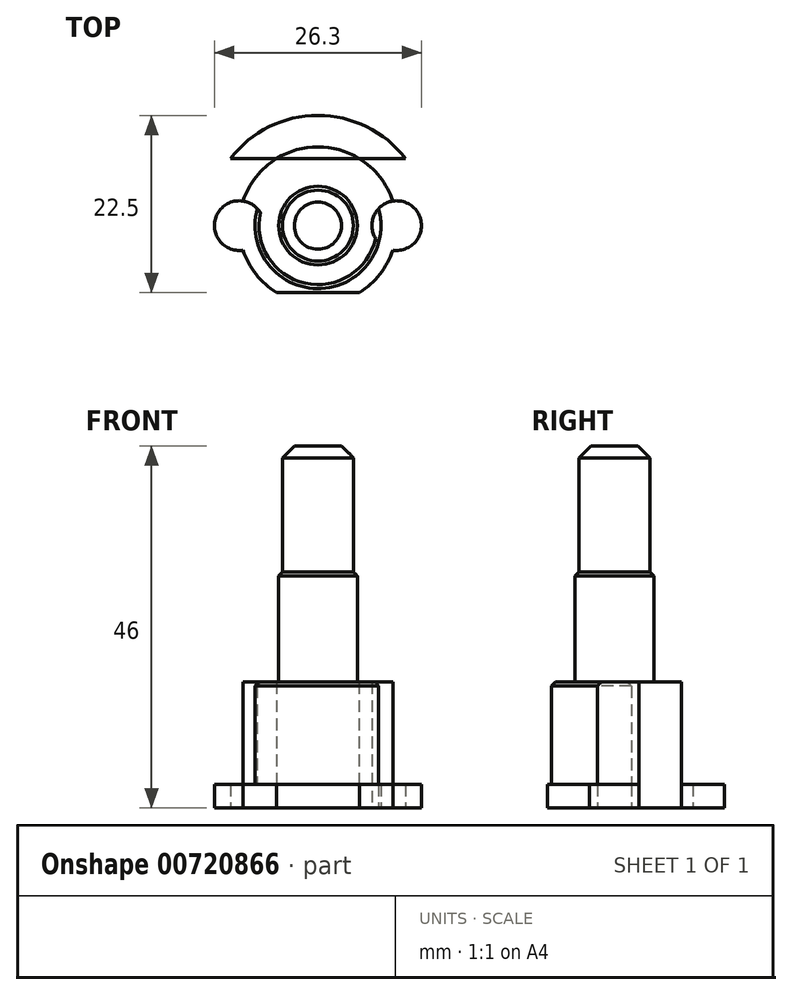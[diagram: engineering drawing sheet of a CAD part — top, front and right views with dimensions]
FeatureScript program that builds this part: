
annotation { "Feature Type Name" : "Feature", "Feature Type Description" : "" }
export const myFeature = defineFeature(function(context is Context, id is Id, definition is map)
    precondition{}
    {
        {
            var Q0;
            Q0=qCreatedBy(makeId("Top.planeOp"),FACE);
            var sketch = newSketch(context, id + "F0", { "sketchPlane" : qUnion([Q0])});
            skCircle(sketch, "E0", {"center": v(0, 0) * mm, "radius": 14 * mm});
            skCircle(sketch, "E1", {"center": v(0, 0) * mm, "radius": 10 * mm});
            skCircle(sketch, "E2", {"center": v(-10, 0) * mm, "radius": 3.15 * mm});
            skCircle(sketch, "E3", {"center": v(-10, 0) * mm, "radius": 1.7 * mm});
            skCircle(sketch, "E4.MirrorC", {"center": v(10, 0) * mm, "radius": 3.15 * mm});
            skCircle(sketch, "E5.MirrorC", {"center": v(10, 0) * mm, "radius": 1.7 * mm});
            skPoint(sketch, "E6", {"position": v(0, 8.5) * mm});
            skPoint(sketch, "E7", {"position": v(0, -8.5) * mm});
            skLineSegment(sketch, "E8", {"start": v(-11.11, 8.52) * mm, "end": v(11.11, 8.52) * mm});
            skLineSegment(sketch, "E9", {"start": v(11.12, -8.5) * mm, "end": v(-11.8, -8.5) * mm});
            skCircle(sketch, "E10", {"center": v(0, 0) * mm, "radius": 8 * mm});
            skSolve(sketch);
        }
        {
            var Q0;
            {var subQ1=sQuery(id+"F0.wireOp",EDGE,"E1");var subQ3=sQuery(id+"F0.wireOp",EDGE,"E4.MirrorC");var subQ11=makeQuery(id+"F0.imprint","INTERSECT",VERTEX,{"disambiguationData":[OD(0.0)],"derivedFrom":[subQ1,subQ3]});Q0=makeQuery(id+"F0.imprint","IMPRINT",FACE,{"disambiguationData":[TD([[makeQuery(id+"F0.imprint","IMPRINT",EDGE,{"disambiguationData":[TD([[subQ11,-1.0]])],"derivedFrom":subQ1}),1.0]])]});}
            var Q1;
            {var subQ0=sQuery(id+"F0.wireOp",EDGE,"E2");var subQ1=sQuery(id+"F0.wireOp",EDGE,"E1");var subQ2=makeQuery(id+"F0.imprint","INTERSECT",VERTEX,{"disambiguationData":[OD(0.0)],"derivedFrom":[subQ1,subQ0]});Q1=makeQuery(id+"F0.imprint","IMPRINT",FACE,{"disambiguationData":[TD([[makeQuery(id+"F0.imprint","IMPRINT",EDGE,{"disambiguationData":[TD([[subQ2,-1.0]])],"derivedFrom":subQ1}),1.0]])]});}
            var Q2;
            {var subQ0=sQuery(id+"F0.wireOp",EDGE,"E3");var subQ1=sQuery(id+"F0.wireOp",EDGE,"E1");var subQ2=makeQuery(id+"F0.imprint","INTERSECT",VERTEX,{"disambiguationData":[OD(0.0)],"derivedFrom":[subQ1,subQ0]});Q2=makeQuery(id+"F0.imprint","IMPRINT",FACE,{"disambiguationData":[TD([[makeQuery(id+"F0.imprint","IMPRINT",EDGE,{"disambiguationData":[TD([[subQ2,-1.0]])],"derivedFrom":subQ1}),1.0]])]});}
            var Q3;
            {var subQ0=sQuery(id+"F0.wireOp",EDGE,"E3");var subQ1=sQuery(id+"F0.wireOp",EDGE,"E1");var subQ2=makeQuery(id+"F0.imprint","INTERSECT",VERTEX,{"disambiguationData":[OD(0.0)],"derivedFrom":[subQ1,subQ0]});Q3=makeQuery(id+"F0.imprint","IMPRINT",FACE,{"disambiguationData":[TD([[makeQuery(id+"F0.imprint","IMPRINT",EDGE,{"disambiguationData":[TD([[subQ2,-1.0]])],"derivedFrom":subQ1}),-1.0]])]});}
            var Q4;
            {var subQ0=sQuery(id+"F0.wireOp",EDGE,"E2");var subQ1=sQuery(id+"F0.wireOp",EDGE,"E1");var subQ2=makeQuery(id+"F0.imprint","INTERSECT",VERTEX,{"disambiguationData":[OD(0.0)],"derivedFrom":[subQ1,subQ0]});Q4=makeQuery(id+"F0.imprint","IMPRINT",FACE,{"disambiguationData":[TD([[makeQuery(id+"F0.imprint","IMPRINT",EDGE,{"disambiguationData":[TD([[subQ2,-1.0]])],"derivedFrom":subQ1}),-1.0]])]});}
            var Q5;
            {var subQ0=sQuery(id+"F0.wireOp",EDGE,"E8");var subQ6=sQuery(id+"F0.wireOp",EDGE,"E0");var subQ10=makeQuery(id+"F0.imprint","INTERSECT",VERTEX,{"disambiguationData":[OD(0.0)],"derivedFrom":[subQ6,subQ0]});Q5=makeQuery(id+"F0.imprint","IMPRINT",FACE,{"disambiguationData":[TD([[makeQuery(id+"F0.imprint","IMPRINT",EDGE,{"disambiguationData":[TD([[subQ10,-1.0]])],"derivedFrom":subQ6}),1.0]])]});}
            var Q6;
            {var subQ4=sQuery(id+"F0.wireOp",EDGE,"E8");var subQ7=sQuery(id+"F0.wireOp",EDGE,"E0");var subQ10=makeQuery(id+"F0.imprint","INTERSECT",VERTEX,{"disambiguationData":[OD(1.0)],"derivedFrom":[subQ7,subQ4]});Q6=makeQuery(id+"F0.imprint","IMPRINT",FACE,{"disambiguationData":[TD([[makeQuery(id+"F0.imprint","IMPRINT",EDGE,{"disambiguationData":[TD([[subQ10,1.0]])],"derivedFrom":subQ7}),1.0]])]});}
            var Q7;
            {var subQ0=sQuery(id+"F0.wireOp",EDGE,"E5.MirrorC");var subQ1=sQuery(id+"F0.wireOp",EDGE,"E1");var subQ2=makeQuery(id+"F0.imprint","INTERSECT",VERTEX,{"disambiguationData":[OD(0.0)],"derivedFrom":[subQ1,subQ0]});Q7=makeQuery(id+"F0.imprint","IMPRINT",FACE,{"disambiguationData":[TD([[makeQuery(id+"F0.imprint","IMPRINT",EDGE,{"disambiguationData":[TD([[subQ2,1.0]])],"derivedFrom":subQ1}),-1.0]])]});}
            var Q8;
            {var subQ0=sQuery(id+"F0.wireOp",EDGE,"E4.MirrorC");var subQ1=sQuery(id+"F0.wireOp",EDGE,"E1");var subQ2=makeQuery(id+"F0.imprint","INTERSECT",VERTEX,{"disambiguationData":[OD(0.0)],"derivedFrom":[subQ1,subQ0]});Q8=makeQuery(id+"F0.imprint","IMPRINT",FACE,{"disambiguationData":[TD([[makeQuery(id+"F0.imprint","IMPRINT",EDGE,{"disambiguationData":[TD([[subQ2,1.0]])],"derivedFrom":subQ1}),-1.0]])]});}
            var Q9;
            {var subQ0=sQuery(id+"F0.wireOp",EDGE,"E5.MirrorC");var subQ1=sQuery(id+"F0.wireOp",EDGE,"E1");var subQ2=makeQuery(id+"F0.imprint","INTERSECT",VERTEX,{"disambiguationData":[OD(0.0)],"derivedFrom":[subQ1,subQ0]});Q9=makeQuery(id+"F0.imprint","IMPRINT",FACE,{"disambiguationData":[TD([[makeQuery(id+"F0.imprint","IMPRINT",EDGE,{"disambiguationData":[TD([[subQ2,1.0]])],"derivedFrom":subQ1}),1.0]])]});}
            var Q10;
            {var subQ0=sQuery(id+"F0.wireOp",EDGE,"E4.MirrorC");var subQ1=sQuery(id+"F0.wireOp",EDGE,"E1");var subQ2=makeQuery(id+"F0.imprint","INTERSECT",VERTEX,{"disambiguationData":[OD(0.0)],"derivedFrom":[subQ1,subQ0]});Q10=makeQuery(id+"F0.imprint","IMPRINT",FACE,{"disambiguationData":[TD([[makeQuery(id+"F0.imprint","IMPRINT",EDGE,{"disambiguationData":[TD([[subQ2,1.0]])],"derivedFrom":subQ1}),1.0]])]});}
            var Q11;
            {var subQ1=sQuery(id+"F0.wireOp",EDGE,"E1");var subQ7=sQuery(id+"F0.wireOp",EDGE,"E2");var subQ8=makeQuery(id+"F0.imprint","INTERSECT",VERTEX,{"disambiguationData":[OD(1.0)],"derivedFrom":[subQ1,subQ7]});Q11=makeQuery(id+"F0.imprint","IMPRINT",FACE,{"disambiguationData":[TD([[makeQuery(id+"F0.imprint","IMPRINT",EDGE,{"disambiguationData":[TD([[subQ8,-1.0]])],"derivedFrom":subQ1}),1.0]])]});}
            var Q12;
            {var subQ0=sQuery(id+"F0.wireOp",EDGE,"E10");var subQ1=sQuery(id+"F0.wireOp",EDGE,"E2");var subQ2=makeQuery(id+"F0.imprint","INTERSECT",VERTEX,{"disambiguationData":[OD(0.0)],"derivedFrom":[subQ1,subQ0]});Q12=makeQuery(id+"F0.imprint","IMPRINT",FACE,{"disambiguationData":[TD([[makeQuery(id+"F0.imprint","IMPRINT",EDGE,{"disambiguationData":[TD([[subQ2,1.0]])],"derivedFrom":subQ1}),-1.0]])]});}
            var Q13;
            {var subQ0=sQuery(id+"F0.wireOp",EDGE,"E10");var subQ1=sQuery(id+"F0.wireOp",EDGE,"E4.MirrorC");var subQ2=makeQuery(id+"F0.imprint","INTERSECT",VERTEX,{"disambiguationData":[OD(0.0)],"derivedFrom":[subQ1,subQ0]});Q13=makeQuery(id+"F0.imprint","IMPRINT",FACE,{"disambiguationData":[TD([[makeQuery(id+"F0.imprint","IMPRINT",EDGE,{"disambiguationData":[TD([[subQ2,1.0]])],"derivedFrom":subQ1}),-1.0]])]});}
            var Q14;
            {var subQ0=sQuery(id+"F0.wireOp",EDGE,"E10");var subQ1=sQuery(id+"F0.wireOp",EDGE,"E2");var subQ2=makeQuery(id+"F0.imprint","INTERSECT",VERTEX,{"disambiguationData":[OD(0.0)],"derivedFrom":[subQ1,subQ0]});Q14=makeQuery(id+"F0.imprint","IMPRINT",FACE,{"disambiguationData":[TD([[makeQuery(id+"F0.imprint","IMPRINT",EDGE,{"disambiguationData":[TD([[subQ2,1.0]])],"derivedFrom":subQ1}),1.0]])]});}
            extrude(context, id + "F1", {"entities" : qUnion([Q0, Q1, Q2, Q3, Q4, Q5, Q6, Q7, Q8, Q9, Q10, Q11, Q12, Q13, Q14]), "depth" : 3 * mm, "offsetDistance" : 25 * mm});
        }
        {
            var Q0;
            {var subQ0=sQuery(id+"F0.wireOp",EDGE,"E10");var subQ1=sQuery(id+"F0.wireOp",EDGE,"E2");var subQ2=makeQuery(id+"F0.imprint","INTERSECT",VERTEX,{"disambiguationData":[OD(0.0)],"derivedFrom":[subQ1,subQ0]});Q0=makeQuery(id+"F0.imprint","IMPRINT",FACE,{"disambiguationData":[TD([[makeQuery(id+"F0.imprint","IMPRINT",EDGE,{"disambiguationData":[TD([[subQ2,1.0]])],"derivedFrom":subQ1}),-1.0]])]});}
            var Q1;
            {var subQ0=sQuery(id+"F0.wireOp",EDGE,"E10");var subQ1=sQuery(id+"F0.wireOp",EDGE,"E2");var subQ2=makeQuery(id+"F0.imprint","INTERSECT",VERTEX,{"disambiguationData":[OD(0.0)],"derivedFrom":[subQ1,subQ0]});Q1=makeQuery(id+"F0.imprint","IMPRINT",FACE,{"disambiguationData":[TD([[makeQuery(id+"F0.imprint","IMPRINT",EDGE,{"disambiguationData":[TD([[subQ2,1.0]])],"derivedFrom":subQ1}),1.0]])]});}
            var Q2;
            {var subQ0=sQuery(id+"F0.wireOp",EDGE,"E10");var subQ1=sQuery(id+"F0.wireOp",EDGE,"E4.MirrorC");var subQ2=makeQuery(id+"F0.imprint","INTERSECT",VERTEX,{"disambiguationData":[OD(0.0)],"derivedFrom":[subQ1,subQ0]});Q2=makeQuery(id+"F0.imprint","IMPRINT",FACE,{"disambiguationData":[TD([[makeQuery(id+"F0.imprint","IMPRINT",EDGE,{"disambiguationData":[TD([[subQ2,1.0]])],"derivedFrom":subQ1}),-1.0]])]});}
            extrude(context, id + "F2", {"entities" : qUnion([Q0, Q1, Q2]), "operationType" : NewBodyOperationType.ADD, "depth" : 16 * mm, "offsetDistance" : 25 * mm});
        }
        {
            var Q0;
            Q0=makeQuery(id+"F2.opExtrude","CAP_FACE",FACE,{"disambiguationData":[OSD([sQuery(id+"F0.wireOp",EDGE,"E10")])],"isStart":false});
            var sketch = newSketch(context, id + "F3", { "sketchPlane" : qUnion([Q0])});
            skCircle(sketch, "E11", {"center": v(0, 0) * mm, "radius": 5 * mm});
            skSolve(sketch);
        }
        {
            var Q0;
            Q0=makeQuery(id+"F3.imprint","IMPRINT",FACE,{"disambiguationData":[TD([[makeQuery(id+"F3.imprint","IMPRINT",EDGE,{"derivedFrom":sQuery(id+"F3.wireOp",EDGE,"E11")}),1.0]])]});
            extrude(context, id + "F4", {"entities" : qUnion([Q0]), "operationType" : NewBodyOperationType.ADD, "depth" : 14 * mm, "offsetDistance" : 25 * mm});
        }
        {
            var Q0;
            Q0=makeQuery(id+"F4.opExtrude","CAP_FACE",FACE,{"disambiguationData":[OSD([sQuery(id+"F3.wireOp",EDGE,"E11")])],"isStart":false});
            var sketch = newSketch(context, id + "F5", { "sketchPlane" : qUnion([Q0])});
            skCircle(sketch, "E12", {"center": v(0, 0) * mm, "radius": 4.5 * mm});
            skSolve(sketch);
        }
        {
            var Q0;
            Q0 = qSketchRegion(id + "F5", true);
            extrude(context, id + "F6", {"entities" : qUnion([Q0]), "operationType" : NewBodyOperationType.ADD, "depth" : 16 * mm, "offsetDistance" : 25 * mm});
        }
        {
            var Q0;
            Q0=makeQuery(id+"F6.opExtrude","CAP_EDGE",EDGE,{"disambiguationData":[OSD([sQuery(id+"F5.wireOp",EDGE,"E12")])],"isStart":false});
            chamfer(context, id + "F7", {"entities" : qUnion([Q0]), "width" : 1.5 * mm, "tangentPropagation" : true});
        }
        {
            var Q0;
            Q0=makeQuery(id+"F2.opExtrude","CAP_EDGE",EDGE,{"disambiguationData":[OSD([sQuery(id+"F0.wireOp",EDGE,"E10")])],"isStart":false});
            var Q1;
            Q1=makeQuery(id+"F4.opExtrude","CAP_EDGE",EDGE,{"disambiguationData":[OSD([sQuery(id+"F3.wireOp",EDGE,"E11")])],"isStart":false});
            chamfer(context, id + "F8", {"entities" : qUnion([Q0, Q1]), "width" : 0.5 * mm, "tangentPropagation" : true});
        }
        {
            var Q0;
            Q0=sQuery(id+"F0.wireOp",VERTEX,"E5.MirrorC.center");
            var Q1;
            Q1=makeQuery(id+"F1.opExtrude","SWEPT_BODY",BODY,{"disambiguationData":[OSD([sQuery(id+"F0.wireOp",EDGE,"E0"),sQuery(id+"F0.wireOp",EDGE,"E8"),sQuery(id+"F0.wireOp",EDGE,"E9")])]});
            hole(context, id + "F9", {"style" : HoleStyle.C_SINK, "endStyle" : HoleEndStyle.THROUGH, "oppositeDirection" : true, "holeDiameter" : 3.4 * mm, "cSinkDiameter" : 6 * mm, "cSinkAngle" : 90 * degree, "majorDiameter" : 5 * mm, "isTappedThrough" : true, "tappedDepth" : 12 * mm, "tapClearance" : 3, "locations" : qUnion([Q0]), "scope" : qUnion([Q1])});
        }
        {
            var Q0;
            Q0=sQuery(id+"F0.wireOp",VERTEX,"E3.center");
            var Q1;
            Q1=makeQuery(id+"F1.opExtrude","SWEPT_BODY",BODY,{"disambiguationData":[OSD([sQuery(id+"F0.wireOp",EDGE,"E0"),sQuery(id+"F0.wireOp",EDGE,"E8"),sQuery(id+"F0.wireOp",EDGE,"E9")])]});
            hole(context, id + "F10", {"style" : HoleStyle.C_SINK, "endStyle" : HoleEndStyle.THROUGH, "oppositeDirection" : true, "holeDiameter" : 3.4 * mm, "cSinkDiameter" : 6 * mm, "cSinkAngle" : 90 * degree, "majorDiameter" : 5 * mm, "isTappedThrough" : true, "tappedDepth" : 12 * mm, "tapClearance" : 3, "locations" : qUnion([Q0]), "scope" : qUnion([Q1])});
        }
    });
